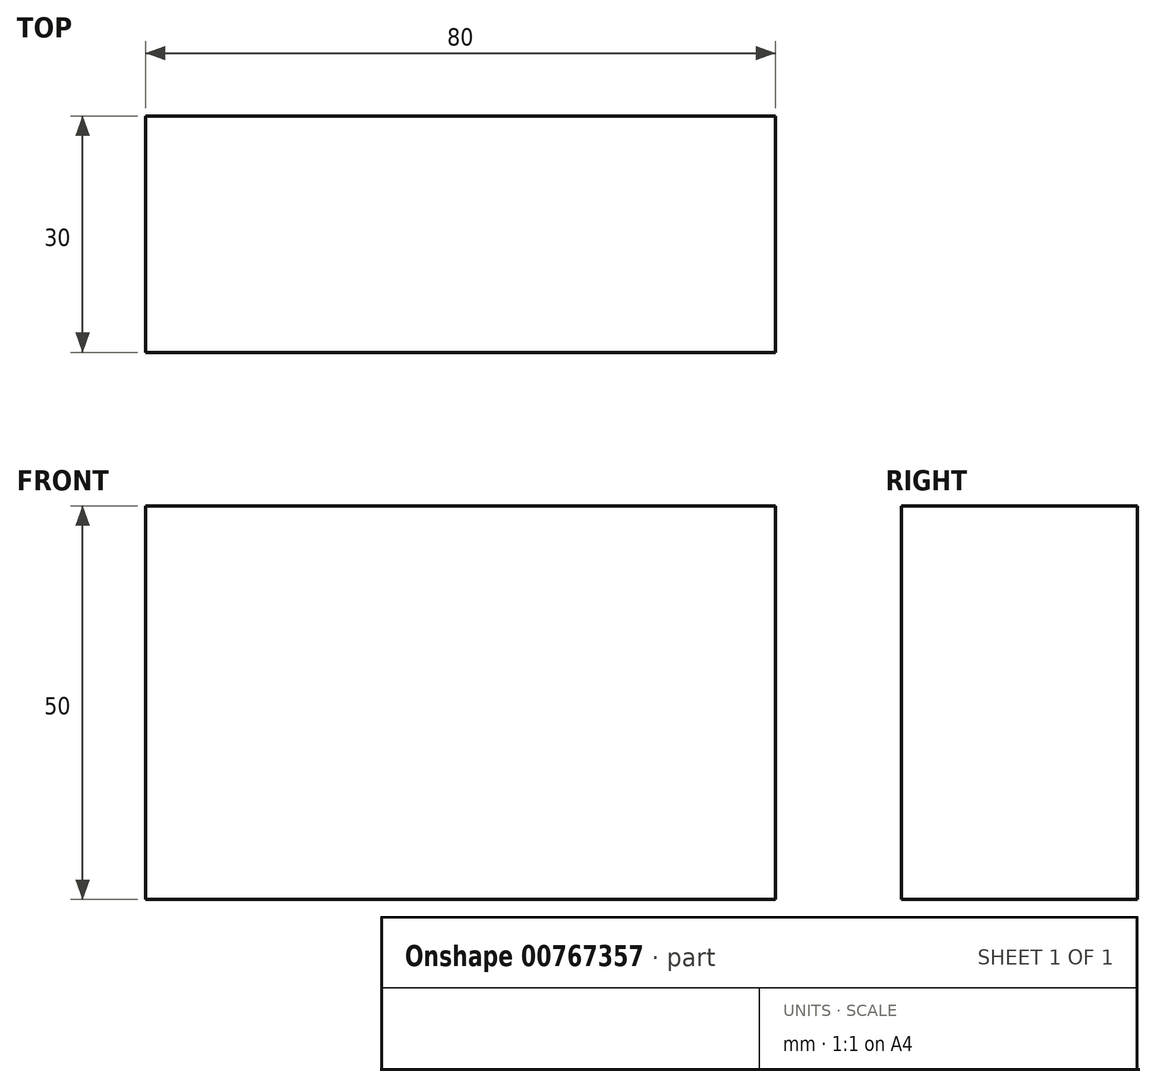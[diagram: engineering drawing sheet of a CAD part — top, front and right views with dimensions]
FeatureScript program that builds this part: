
annotation { "Feature Type Name" : "Feature", "Feature Type Description" : "" }
export const myFeature = defineFeature(function(context is Context, id is Id, definition is map)
    precondition{}
    {
        {
            var Q0;
            Q0=qCreatedBy(makeId("Front.planeOp"),FACE);
            var sketch = newSketch(context, id + "F0", { "sketchPlane" : qUnion([Q0])});
            skLineSegment(sketch, "E0.bottom", {"start": v(-44.92, -29.5) * mm, "end": v(35.08, -29.5) * mm});
            skLineSegment(sketch, "E0.top", {"start": v(-44.92, 20.5) * mm, "end": v(35.08, 20.5) * mm});
            skLineSegment(sketch, "E0.left", {"start": v(-44.92, -29.5) * mm, "end": v(-44.92, 20.5) * mm});
            skLineSegment(sketch, "E0.right", {"start": v(35.08, -29.5) * mm, "end": v(35.08, 20.5) * mm});
            skSolve(sketch);
        }
        {
            var Q0;
            Q0 = qSketchRegion(id + "F0", true);
            extrude(context, id + "F1", {"entities" : qUnion([Q0]), "depth" : 30 * mm, "offsetDistance" : 25 * mm});
        }
    });
